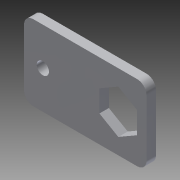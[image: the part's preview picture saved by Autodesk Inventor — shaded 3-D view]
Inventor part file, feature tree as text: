
AUTODESK INVENTOR PART (.ipt)
format: ipt  version: 2014 (Build 180170000, 170)  size: 95,232 bytes
history: native  units: in
note: dims shown in document units (in); Inventor stores cm internally (conversion verified against a paired STEP export)
features: extrude x1, fillet x1, sketch x1
ambient origin geometry x8: Origin, YZ Plane, XZ Plane, XY Plane, X Axis, Y Axis, Z Axis, Center Point
bodies: Solid1 (feature_tree)
feature tree (3):
  extrude  "Extrusion1"  Depth=1.0in
  fillet  "Fillet1"  Radius=0.163in
  sketch  "Sketch1"  dims[d0=1.625in d1=1.0in d2=0.163in d3=0.5in d4=0.25in d5=1.0in d6=0.5in d7=0.5in d8=0.125in d9=0.0in d10=0.125in]
